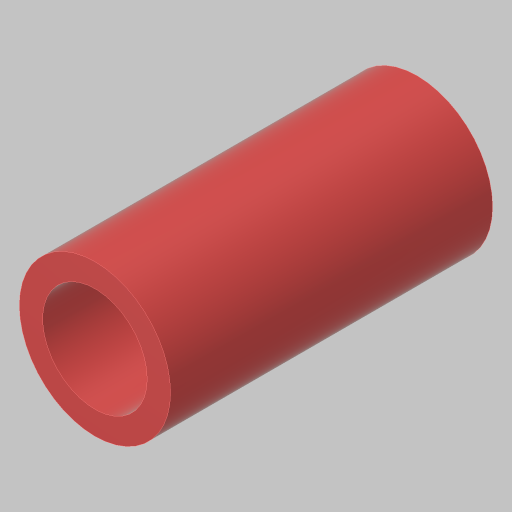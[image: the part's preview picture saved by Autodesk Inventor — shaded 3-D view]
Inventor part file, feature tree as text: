
AUTODESK INVENTOR PART (.ipt)
format: ipt  version: 2023.5 (Build 275446000, 446)  size: 116,736 bytes
history: native  units: in
note: dims shown in document units (in); Inventor stores cm internally (conversion verified against a paired STEP export)
features: extrude x1, sketch x1
ambient origin geometry x8: Origin, YZ Plane, XZ Plane, XY Plane, X Axis, Y Axis, Z Axis, Center Point
bodies: Solid1 (feature_tree)
feature tree (2):
  extrude  "Extrusion1"  Depth=1.725in
  sketch  "Sketch1"  dims[d0=0.56in d1=0.125in d2=1.725in d3=0.0in]
